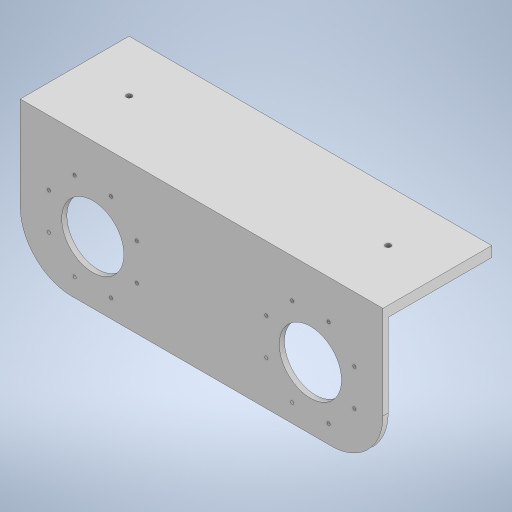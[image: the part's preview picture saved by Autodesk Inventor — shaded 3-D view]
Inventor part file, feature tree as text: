
AUTODESK INVENTOR PART (.ipt)
format: ipt  version: 2024.3 (Build 283343000, 343)  size: 273,920 bytes
history: native  units: mm
features: extrude x3, sketch x3, other x1, fillet x1
ambient origin geometry x8: Origin, YZ Plane, XZ Plane, XY Plane, X Axis, Y Axis, Z Axis, Center Point
bodies: Body1 (feature_tree)
feature tree (8):
  other  "ソリッド1"
  extrude  "押し出し1"  Depth=350.0mm
  extrude  "押し出し2"  Depth=140.0mm
  extrude  "押し出し3"  Depth=60.0mm
  fillet  "フィレット2"  Radius=60.0mm
  sketch  "スケッチ1"
  sketch  "スケッチ2"
  sketch  "スケッチ3"
